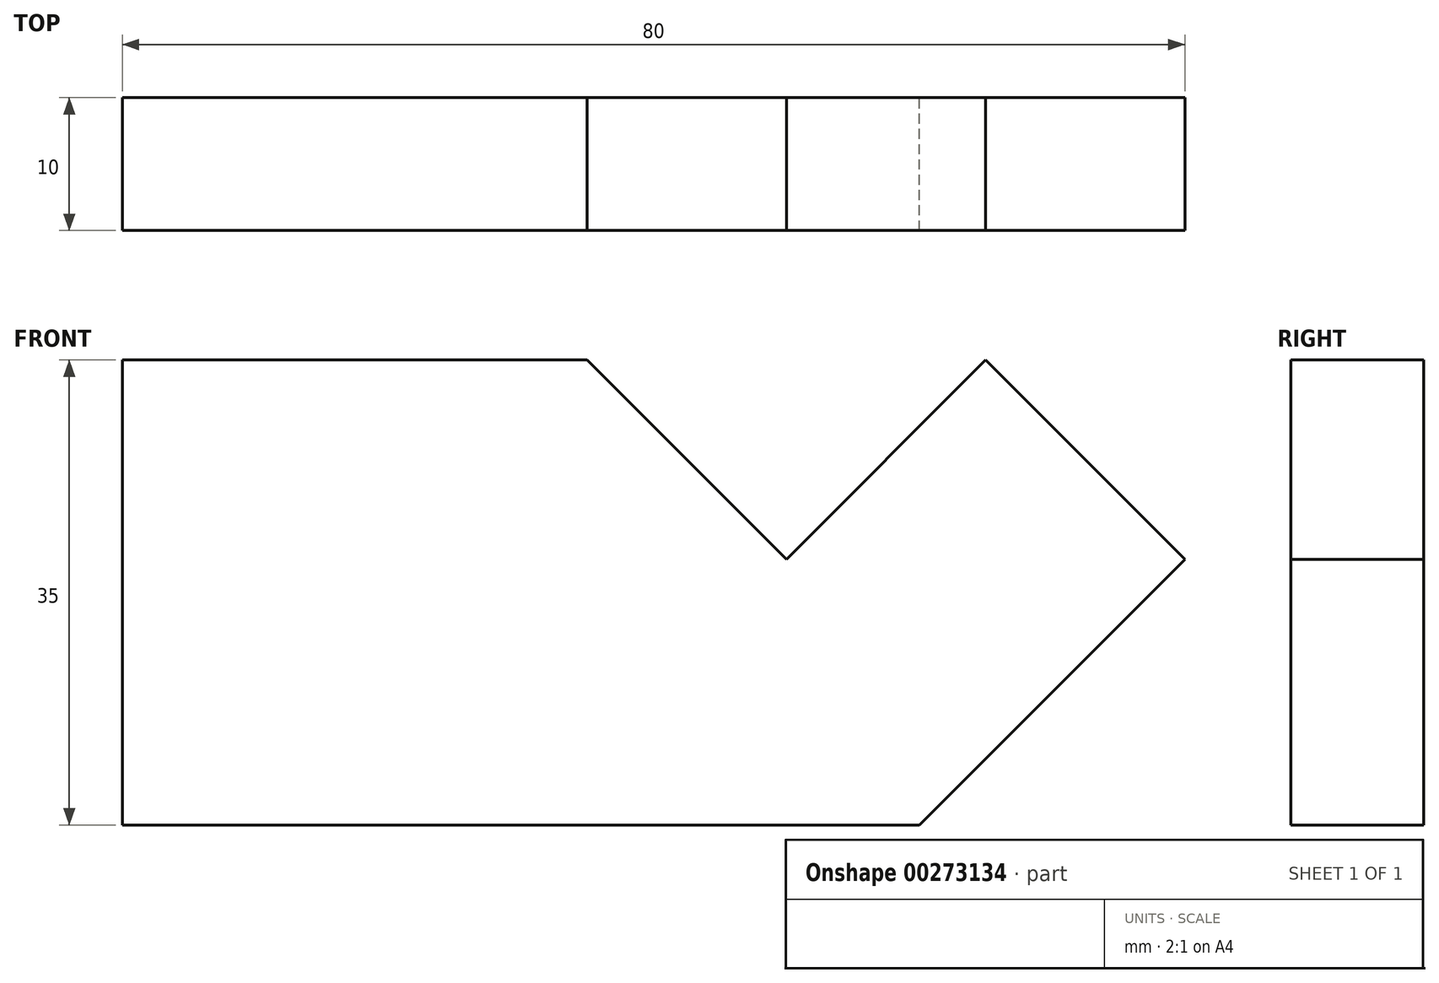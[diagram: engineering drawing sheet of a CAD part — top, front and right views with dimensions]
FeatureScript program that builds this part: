
annotation { "Feature Type Name" : "Feature", "Feature Type Description" : "" }
export const myFeature = defineFeature(function(context is Context, id is Id, definition is map)
    precondition{}
    {
        {
            var Q0;
            Q0=qCreatedBy(makeId("Front.planeOp"),FACE);
            var sketch = newSketch(context, id + "F0", { "sketchPlane" : qUnion([Q0])});
            skLineSegment(sketch, "E0", {"start": v(0, 0) * mm, "end": v(0, 35) * mm});
            skLineSegment(sketch, "E1", {"start": v(60, 0) * mm, "end": v(80, 20) * mm});
            skLineSegment(sketch, "E2", {"start": v(50, 20) * mm, "end": v(65, 35) * mm});
            skLineSegment(sketch, "E3", {"start": v(65, 35) * mm, "end": v(80, 20) * mm});
            skLineSegment(sketch, "E4", {"start": v(50, 20) * mm, "end": v(35, 35) * mm});
            skLineSegment(sketch, "E5", {"start": v(0, 35) * mm, "end": v(35, 35) * mm});
            skLineSegment(sketch, "E6", {"start": v(0, 0) * mm, "end": v(60, 0) * mm});
            skSolve(sketch);
        }
        {
            var Q0;
            Q0 = qSketchRegion(id + "F0", true);
            extrude(context, id + "F1", {"entities" : qUnion([Q0]), "depth" : 10 * mm});
        }
    });
